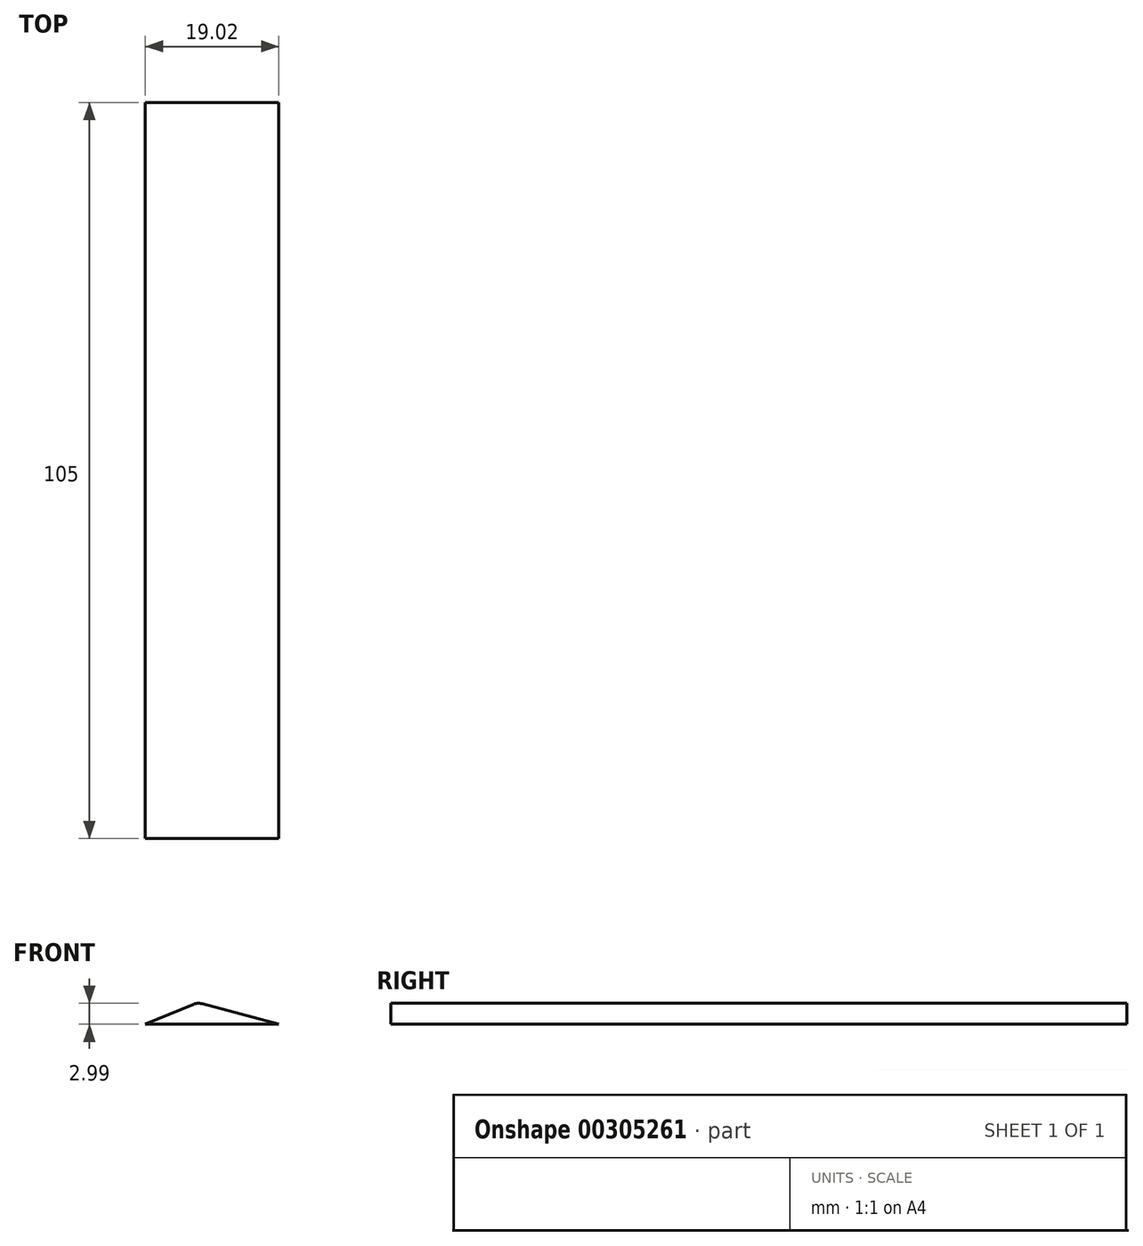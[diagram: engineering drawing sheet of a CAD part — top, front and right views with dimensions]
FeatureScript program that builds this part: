
annotation { "Feature Type Name" : "Feature", "Feature Type Description" : "" }
export const myFeature = defineFeature(function(context is Context, id is Id, definition is map)
    precondition{}
    {
        {
            var Q0;
            Q0=qCreatedBy(makeId("Front.planeOp"),FACE);
            var sketch = newSketch(context, id + "F0", { "sketchPlane" : qUnion([Q0])});
            skLineSegment(sketch, "E0", {"start": v(0, 0) * mm, "end": v(-19.02, 0) * mm});
            skLineSegment(sketch, "E1", {"start": v(-19.02, 0) * mm, "end": v(-12.21, 2.84) * mm});
            skLineSegment(sketch, "E2", {"start": v(-10.93, 2.92) * mm, "end": v(0, 0) * mm});
            skPoint(sketch, "E3.visualSharp", {"position": v(-11.58, 3.1) * mm});
            skArc(sketch, "E3.filletArc", {"start": v(-10.93, 2.92) * mm, "mid": v(-11.58, 2.99) * mm, "end": v(-12.21, 2.84) * mm});
            skSolve(sketch);
        }
        {
            var Q0;
            Q0=makeQuery(id+"F0.imprint","IMPRINT",FACE,{"disambiguationData":[TD([[makeQuery(id+"F0.imprint","IMPRINT",EDGE,{"derivedFrom":sQuery(id+"F0.wireOp",EDGE,"E0")}),-1.0]])]});
            extrude(context, id + "F1", {"entities" : qUnion([Q0]), "depth" : 105 * mm});
        }
    });
